# Revit family: HVAC_Mechanical-Ventilation_Ice-Air_WSHP_Horizontal
name_source: partatom
category: Mechanical Equipment
revit_build: Autodesk Revit 2015 (Build: 20140606_1530(x64)
units: mm (PartAtom-declared; Revit-internal decimal feet)

## types (11) — shared parameters
2-pipe Inlet Description = Water Inlet Connection
2-pipe Outlet Description = Water Outlet Connection
Air Filter Material = Plastic - Ice_Air - Blue
BIMobject category = Air Conditioning
BIMobject category code = hvac-air-con
BIMobject main category = HVAC
BIMobject main category code = hvac
Brand url = http://www.ice-air.com
Condensate Connection = 0.75 "
Condensate Drain Description = Condensate Drain Connection
Date of publishing = 1/13/2014
Default Elevation = 48 "
Description = Conserve floor space with ICE AIRs Horizontal WSHPs - flexible control options, variable air discharge outlets, and easy service access provide superior design and installation options.
Design country = United States
Discharge Position = 12 "
Duct Description = Supply Air
Edition number = 1
Frequency = 60 Hz
IFC Classification = Heat Exchanger
Manufacturer = Ice Air
Manufacturer country = United States
Manufacturer name = Ice Air
Masterformat 2014 Code = 23 81 46
Masterformat 2014 Description = Water-Source Unitary Heat Pumps
NBS Reference Code = 68-38
NBS Reference Description = Heat Pumps
OmniClass Code = 23-33 17 00
OmniClass Description = Heat Pumps
Phase = 1
Product Guid = b4406440-e514-438c-8a19-9ec2fd8eca6f
Product SKU = horizontal_wshp
Product data url = https://bimobject.com
Product family = WSHP
Product group = Horizontal
Product url = http://www.ice-air.com
QR code = http://bimobject.com
Return Lenght = 25.4 "
Return Offset = 1.54 "
Steel Material = Steel - Ice_Air - Galvanized
Technical description = http://www.ice-air.com
UNSPSC Code = 40101806
URL = http://www.ice-air.com
Uniclass 1.4 Code = L7524
Uniclass 1.4 Description = Heat pumps
Uniclass 2.0 Code = PR-68-38
Uniclass 2.0 Description = Heat Pumps
Uniclass 2015 Code = Pr_70_60_37
Uniclass 2015 Name = Heat pumps
Uniformat II Code = D3090
Uniformat II Description = Other HVAC Systems & Equipment
Voltage = 230 V
Voltage (Range) = 208 - 230 V
Weight Net (Kg) = 0
zero-valued in all types: Nominal height, Nominal width

## per-type parameters (varying)
| type | Air Flow | Coefficient of Performance | Cooling Coil Water Pressure Drop | Discharge Height | Discharge Width | Energy Efficiency Rating w/PSC | Flow Rate | Height | Inlet/Outlet Connection | Length | Total Cooling Capacity | Total Heating Capacity | Weight | Width | z Type |
| 8HHPW09 | 300.0 CFM | 4.8 | 3.1 psi | 5 " | 10 " | 14 | 2.3 GPM | 12 " | 0.5 " | 34 " | 9300 Btu/h | 11000 Btu/h | 130 lbm | 20 " | 1 |
| 8HHPW12 | 400.0 CFM | 4.5 | 2.8 psi | 5 " | 10 " | 13.5 | 3.0 GPM | 12 " | 0.5 " | 34 " | 12200 Btu/h | 14500 Btu/h | 140 lbm | 20 " | 2 |
| 8HHPW15 | 500.0 CFM | 4.5 | 4.4 psi | 8 " | 9 " | 14.3 | 3.8 GPM | 17 " | 0.5 " | 42 " | 14900 Btu/h | 17200 Btu/h | 180 lbm | 20 " | 3 |
| 8HHPW18 | 600.0 CFM | 4.8 | 3.9 psi | 8 " | 9 " | 14 | 4.5 GPM | 17 " | 0.75 " | 42 " | 19500 Btu/h | 22000 Btu/h | 220 lbm | 20 " | 4 |
| 8HHPW24 | 800.0 CFM | 4.8 | 6.4 psi | 10 " | 11 " | 14.4 | 6.0 GPM | 18.25 " | 0.75 " | 42 " | 23500 Btu/h | 29500 Btu/h | 280 lbm | 20 " | 5 |
| 8HHPW30 | 1000.0 CFM | 4.7 | 6.5 psi | 10 " | 11 " | 14.5 | 7.5 GPM | 18.25 " | 0.75 " | 42 " | 29100 Btu/h | 35500 Btu/h | 300 lbm | 20 " | 6 |
| 8HHPW36 | 1200.0 CFM | 4.7 | 4.6 psi | 11 " | 12 " | 15 | 9.0 GPM | 20 " | 0.75 " | 46 " | 35000 Btu/h | 42000 Btu/h | 310 lbm | 21 " | 7 |
| 8HHPW42 | 1400.0 CFM | 4.6 | 6.3 psi | 11 " | 12 " | 14.2 | 10.5 GPM | 20 " | 0.75 " | 46 " | 41500 Btu/h | 46500 Btu/h | 320 lbm | 21 " | 8 |
| 8HHPW48 | 1600.0 CFM | 4.4 | 8.3 psi | 12 " | 13 " | 13.8 | 12.0 GPM | 23 " | 0.75 " | 52 " | 48300 Btu/h | 55000 Btu/h | 330 lbm | 28 " | 9 |
| 8HHPW60 | 2000.0 CFM | 4.6 | 7.7 psi | 12 " | 13 " | 14.2 | 15.0 GPM | 23 " | 0.75 " | 52 " | 60000 Btu/h | 71500 Btu/h | 350 lbm | 28 " | 10 |
| 8HHPW70 | 2400.0 CFM | 4.5 | 10.3 psi | 12 " | 13 " | 14 | 17.5 GPM | 23 " | 0.75 " | 52 " | 67000 Btu/h | 77000 Btu/h | 380 lbm | 28 " | 11 |

note: column(s) folded — value = type name in every type: Model

## geometry (parser evidence)
native form markers: Sweep x16
no freeform markers — native parametric forms only
